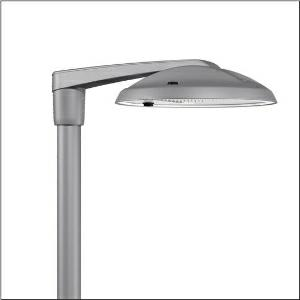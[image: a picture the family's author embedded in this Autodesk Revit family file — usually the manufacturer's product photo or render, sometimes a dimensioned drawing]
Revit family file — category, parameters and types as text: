
# Revit family: dl_r__50_iq_mini___st1_0a_5xa248d31y08ne_98a7
name_source: partatom
category: Lighting Fixtures
units: mm (PartAtom-declared; Revit-internal decimal feet)

## family parameters
Cut with Voids When Loaded = No
Host = Face
Light Source = No
Part Type = Normal
Room Calculation Point = No
Round Connector Dimension = Use Diameter
Shared = No

## types (1)
- --- (1 x LED, 17900 lm, 110.1 W, 3000K)
    Apparent Load = 110 VA
    CIE Flux Codes = 37 72 97 100 100
    Color Rendering = 70
    Color Temperature = 3000K
    Default Elevation = 1800 mm
    Description = DL® 50 iQ mini, mast luminaire, primary light control with lens, of PMMA, primary optical cover: cover, of toughened safety glass, transparent, light distribution: ST1.0a, light emission: direct distribution, primary light characteristic: asymmetric, installation type: post-top, side-entry, LED, High Power LED, rated luminous flux: 17.900lm, luminous efficacy: 163lm/W, light colour: 730, colour temperature: 3000K, control gear: iQ-Street Remote, D4i with power reduction, control: optimised constant luminous flux control (CLO 2.0), Desk-Remote (wireless, voltage-free reading and setting of iQ features in the workshop via application-optimized NFC function/RFID function), Light-Fading, Smart-Wire, Night-Set, Lumen-Switch, Temp-Guard, Auto-Match, Street-Remote, pre-setting: logarithmic dimming characteristic, mains connection: 230..240V, AC, 50/60Hz, connection cable pre-assembled, cable length: 10,5m, start of lifetime: 110W, end of service life: 116W, reduction: 50W, luminaire housing, of diecast aluminium, powder-coated, Siteco® metallic grey (DB 702S), inclination adjustable: 0°, 5°, 10° (post-top) | 0°, -5°, -10°, -15° (side-entry), please order mast post-top element or mast side-entry element separately, diameter: 500mm, height: 115mm, post-top: for spigot size d x l = 76 x 100mm; with reducer (optional accessory) 60 x 100mm | side-entry: for spigot size d x l = 60 x 100mm; with reducer (optional accessory) 42 x 100mm, mounting height: 4..6m, Smart Interface below and above, protection rating (complete): IP66, insulation class (complete): insulation class II (safety insulation), certification: CE, ENEC, ENEC+, VDE, impact resistance: IK08, permissible operating ambient temperature for outdoor applications: -25..+40°C, standard-compliant lighting for roads and squares, packaging unit: 1 piece

Light Distribution: ST1.0a
    Height = 115 mm
    Lamp = 1 x LED
    Lamp Light Flux = 17900 lm
    Lamp Power = 110.1 W
    Lamp count = 1
    Length = 500 mm
    Luminous efficacy = 163 lm/W
    Manufacturer = Siteco
    ModVariant = No
    Model = 5XA248D31Y08NE
    Number of Poles = 1
    OnlyDefault = Yes
    Power Factor = 1
    Product Name = DL® 50 iQ mini | ST1.0a
    Product group = mast luminaire | pylon top
    ProductGroupID = 6100
    Protection Class = Protection class II
    Protection Degree = IP 66
    RLX_Detail_Level = 1
    RLX_Emergency_Light_Flux = 0 lm
    RLX_Emergency_Type = 0
    RLX_Emergency_Type_DB = No
    RlxData = <blob elided: 106645 chars, md5=3b021d25>
    Socket = socket
    Standby Power = 0 W
    System Light Flux = 17900 lm
    System Power = 110 W
    Type Comments = factory setting: luminous flux: 100 % | dim-lin: 254 | 601 mA
    Type Image = l_1251786.jpg
    URL = http://relux.com
    VarID = @adj_086547
    Voltage = 0 V
    Weight = 0.00 kg
    Width = 0 mm  [stored 0 ft]

note: [stored X ft] marks values corroborated as IEEE doubles in the binary element streams (Revit-internal decimal feet)

## geometry (parser evidence)
native form markers: Blend x4, Sweep x9
no freeform markers — native parametric forms only
